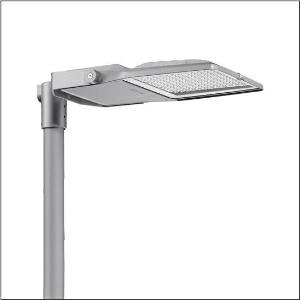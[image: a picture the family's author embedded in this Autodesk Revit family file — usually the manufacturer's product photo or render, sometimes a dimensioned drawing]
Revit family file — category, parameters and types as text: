
# Revit family: floodlight_fl_21_iq_midi___pl61_5xa7781f4c3a_8dc1
name_source: partatom
category: Lighting Fixtures
units: mm (PartAtom-declared; Revit-internal decimal feet)

## family parameters
Cut with Voids When Loaded = No
Host = Face
Light Source = No
Part Type = Normal
Room Calculation Point = No
Round Connector Dimension = Use Diameter
Shared = No

## types (1)
- --- (1 x LED, 36650 lm, 270.2 W, 4000K)
    Apparent Load = 270 VA
    CIE Flux Codes = 33 65 98 100 100
    Color Rendering = 70
    Color Temperature = 4000K
    Default Elevation = 1800 mm
    Description = Floodlight FL 21 iQ midi, floodlight, primary light control with lens, of PMMA, primary optical cover: protective disc, of toughened safety glass, transparent, light distribution: PL61, light emission: direct distribution, installation type: surface-mounted, LED, High Power LED, rated luminous flux: 36.650lm, luminous efficacy: 136lm/W, light colour: 740, colour temperature: 4000K, control gear: ECG iQ, control: optimised constant luminous flux control (CLO 2.0), Desk-Remote (wireless, voltage-free reading and setting of iQ features in the workshop via application-optimized NFC function/RFID function), Light-Fading, Smart-Wire, Night-Set, Lumen-Switch, Temp-Guard, Auto-Match, with terminal, 6-pole, mains connection: 220..240V, AC, 50/60Hz, start of lifetime: 270W, end of service life: 287W, reduction: 118W, luminaire housing, of diecast aluminium, powder-coated, Siteco® metallic grey (DB 702S), corrosivity category C5 mid according to DIN EN ISO 12944, sealing non-destructively replaceable, please order mast flange separately, mast bracket, of steel, galvanised, powder-coated, Siteco® metallic grey (DB 702S), protection rating (complete): IP66, insulation class (complete): insulation class II (safety insulation), certification: CE, protection symbol: D, impact resistance: IK08, permissible operating ambient temperature: -40..+40°C, permissible operating ambient temperature for outdoor applications: -40..+50°C, standard: DIN EN 12944, LABS conformity tested according to VDMA 24364:2018-05, packaging unit: 1 piece

Light Distribution: PL61
    Height = 76 mm
    Lamp = 1 x LED
    Lamp Light Flux = 36650 lm
    Lamp Power = 270.2 W
    Lamp count = 1
    Length = 657 mm
    Luminous efficacy = 136 lm/W
    Manufacturer = Siteco
    ModVariant = No
    Model = 5XA7781F4C3A
    Number of Poles = 1
    OnlyDefault = Yes
    Power Factor = 1
    Product Name = Floodlight FL 21 iQ midi | PL61
    Product group = floodlight | pylon annexe
    ProductGroupID = 6200
    Protection Class = Protection class II
    Protection Degree = IP 66
    RLX_Detail_Level = 1
    RLX_Emergency_Light_Flux = 0 lm
    RLX_Emergency_Type = 0
    RLX_Emergency_Type_DB = No
    RlxData = <blob elided: 153717 chars, md5=a752b4cd>
    Socket = socket
    Standby Power = 0 W
    System Light Flux = 36650 lm
    System Power = 270 W
    Type Comments = factory setting: luminous flux: 100 % | dim-lin: 254 | 620 mA
    Type Image = l_1007123.jpg
    URL = http://relux.com
    VarID = @adj_056697
    Voltage = 0 V
    Weight = 0.00 kg
    Width = 442 mm

## geometry (parser evidence)
native form markers: Blend x4, Sweep x13
no freeform markers — native parametric forms only
